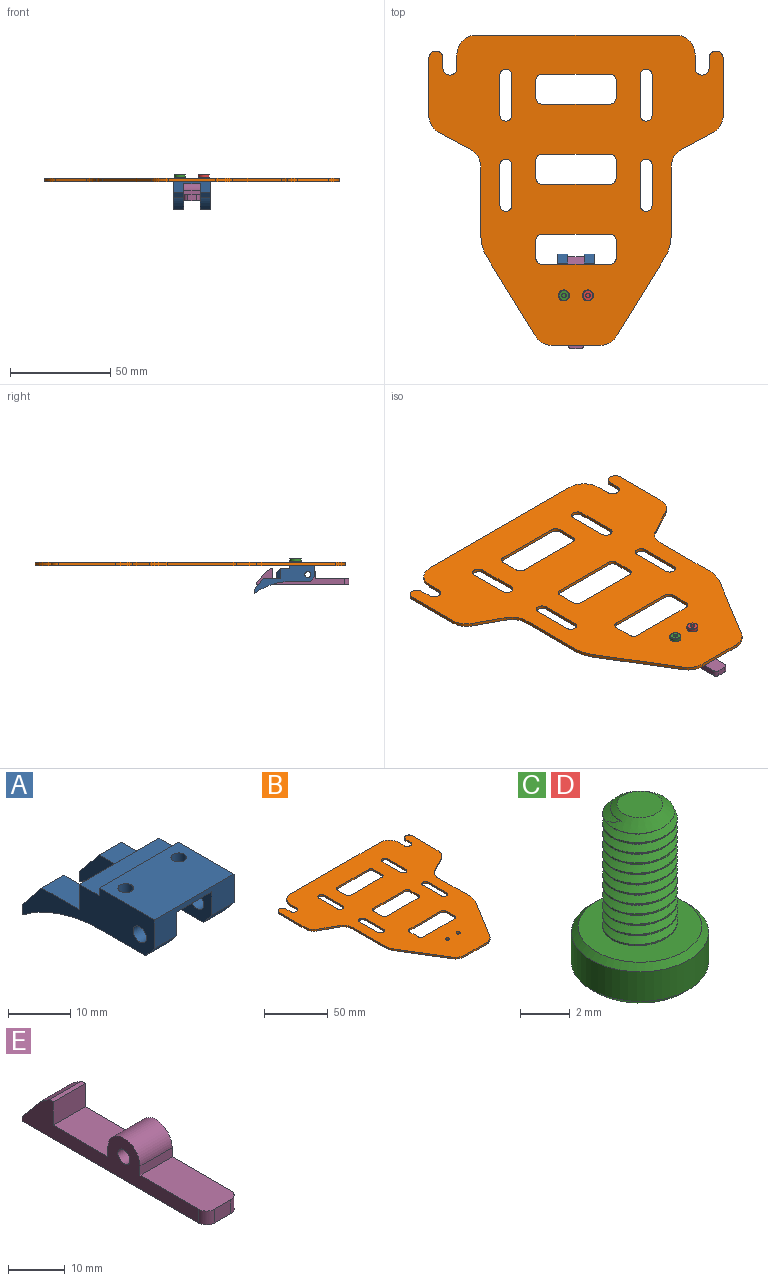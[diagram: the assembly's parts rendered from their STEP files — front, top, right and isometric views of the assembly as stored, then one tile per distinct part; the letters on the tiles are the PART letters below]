
ASSEMBLY  parts=5 mates=3
PART A: 31 faces, bbox 18x30x14 mm
  f0: plane 8.5x5mm, normal (0,0,1), area 34.5mm2, adj f4,f9,f20,f25,f29
  f1: plane 5x2.38mm, normal (0,-0.77,-0.64), area 15.6mm2, adj f2,f6,f20,f25
  f2: plane 10x5mm, normal (0,0,-1), area 45.1mm2, adj f1,f7,f20,f25,f27
  f3: plane 5x2mm, normal (0,1,0), area 10mm2, adj f4,f7,f20,f25
  f4: plane 5.5x5mm, normal (0,0.77,0.63), area 35.5mm2, adj f0,f3,f20,f25
  f5: cylinder r=1.5mm len=5mm, axis (-1,0,0), area 47.1mm2, adj f20,f25
  f6: plane 18x5.62mm, normal (0,-1,0), area 64.2mm2, adj f1,f12,f13,f19,f20,f21,f24,f25
  f7: cylinder r=30mm len=18mm, axis (-1,0,0), area 96.5mm2, adj f2,f3,f20,f25
  f8: plane 8.5x5mm, normal (0,0,1), area 34.5mm2, adj f9,f17,f19,f24,f28
  f9: plane 14x3mm, normal (0,1,0), area 42mm2, adj f0,f8,f22,f28,f29,f30
  f10: plane 18x4.5mm, normal (0,0,1), area 81mm2, adj f11,f19,f20,f30
  f11: plane 18x1.5mm, normal (0,1,0), area 27mm2, adj f10,f12,f19,f20
  f12: plane 18x12.5mm, normal (0,0,1), area 215.2mm2, adj f6,f11,f19,f20,f26,f27
  f13: plane 5x2.38mm, normal (0,-0.77,-0.64), area 15.6mm2, adj f6,f14,f19,f24
  f14: plane 10x5mm, normal (0,0,-1), area 45.1mm2, adj f13,f15,f19,f24,f26
  f15: cylinder r=30mm len=18mm, axis (-1,0,0), area 96.5mm2, adj f14,f16,f19,f24
  f16: plane 5x2mm, normal (0,1,0), area 10mm2, adj f15,f17,f19,f24
  f17: plane 5.5x5mm, normal (0,0.77,0.63), area 35.5mm2, adj f8,f16,f19,f24
  f18: cylinder r=1.5mm len=5mm, axis (-1,0,0), area 47.1mm2, adj f19,f24
  f19: plane 30x14mm, normal (1,0,0), area 161.3mm2, adj f6,f8,f10,f11,f12,f13,f14,f15
  f20: plane 30x14mm, normal (-1,0,0), area 161.3mm2, adj f0,f1,f2,f3,f4,f5,f6,f7
  f21: plane 10x8mm, normal (0,0,-1), area 80mm2, adj f6,f23,f24,f25
  f22: plane 9x8mm, normal (0,0,-1), area 72mm2, adj f9,f23,f24,f25
  f23: plane 8x5.5mm, normal (0,-1,0), area 44mm2, adj f21,f22,f24,f25
  f24: plane 30x13mm, normal (-1,0,0), area 112.6mm2, adj f6,f8,f13,f14,f15,f16,f17,f18
  f25: plane 30x13mm, normal (1,0,0), area 112.6mm2, adj f0,f1,f2,f3,f4,f5,f6,f7
  f26: cylinder r=1.25mm len=8mm, axis (0,0,1), area 62.8mm2, adj f12,f14
  f27: cylinder r=1.25mm len=8mm, axis (0,0,1), area 62.8mm2, adj f2,f12
  f28: plane 5x2mm, normal (0.71,0.71,0), area 11.3mm2, adj f8,f9,f19,f30
  f29: plane 5x2mm, normal (-0.71,0.71,0), area 11.3mm2, adj f0,f9,f20,f30
  f30: plane 18x2mm, normal (0,0.71,0.71), area 45.3mm2, adj f9,f10,f28,f29
PART B: 72 faces, bbox 147x155x1.6 mm
  f0: cylinder r=3mm len=6mm, axis (0,0,-1), area 14.6mm2, adj f1,f67,f68,f69
  f1: plane 20x1.55mm, normal (-1,0,0), area 31mm2, adj f0,f2,f68,f69
  f2: cylinder r=3mm len=6mm, axis (0,0,-1), area 14.6mm2, adj f1,f67,f68,f69
  f3: plane 20x1.55mm, normal (-1,0,0), area 31mm2, adj f4,f60,f68,f69
  f4: cylinder r=3mm len=6mm, axis (0,0,-1), area 14.6mm2, adj f3,f5,f68,f69
  f5: plane 20x1.55mm, normal (1,0,0), area 31mm2, adj f4,f60,f68,f69
  f6: plane 20x1.55mm, normal (-1,0,0), area 31mm2, adj f7,f61,f68,f69
  f7: cylinder r=3mm len=6mm, axis (0,0,-1), area 14.6mm2, adj f6,f8,f68,f69
  f8: plane 20x1.55mm, normal (1,0,0), area 31mm2, adj f7,f61,f68,f69
  f9: cylinder r=10mm len=8.53mm, axis (0,0,-1), area 15.8mm2, adj f10,f62,f68,f69
  f10: plane 39.41x24.13mm, normal (0.85,-0.52,0), area 71.6mm2, adj f9,f11,f68,f69
  f11: cylinder r=20mm len=10.44mm, axis (0,0,-1), area 17mm2, adj f10,f12,f68,f69
  f12: plane 34.39x1.55mm, normal (1,0,0), area 53.3mm2, adj f11,f13,f68,f69
  f13: cylinder r=10mm len=8.8mm, axis (0,0,-1), area 16.7mm2, adj f12,f14,f68,f69
  f14: plane 15.48x8.34mm, normal (0.47,-0.88,0), area 27.3mm2, adj f13,f15,f68,f69
  f15: cylinder r=10mm len=8.8mm, axis (0,0,-1), area 16.7mm2, adj f14,f16,f68,f69
  f16: plane 28.53x1.55mm, normal (1,0,0), area 44.2mm2, adj f15,f17,f68,f69
  f17: cylinder r=3.5mm len=7mm, axis (0,0,-1), area 17mm2, adj f16,f18,f68,f69
  f18: plane 5x1.55mm, normal (-1,0,0), area 7.7mm2, adj f17,f19,f68,f69
  f19: cylinder r=3.5mm len=7mm, axis (0,0,-1), area 17mm2, adj f18,f20,f68,f69
  f20: plane 6.5x1.55mm, normal (1,0,0), area 10.1mm2, adj f19,f21,f68,f69
  f21: cylinder r=10mm len=10mm, axis (0,0,-1), area 24.3mm2, adj f20,f22,f68,f69
  f22: plane 99x1.55mm, normal (0,1,0), area 153.5mm2, adj f21,f23,f68,f69
  f23: cylinder r=10mm len=10mm, axis (0,0,-1), area 24.3mm2, adj f22,f24,f68,f69
  f24: plane 6.5x1.55mm, normal (-1,0,0), area 10.1mm2, adj f23,f25,f68,f69
  f25: cylinder r=3.5mm len=7mm, axis (0,0,-1), area 17mm2, adj f24,f26,f68,f69
  f26: plane 5x1.55mm, normal (1,0,0), area 7.7mm2, adj f25,f27,f68,f69
  f27: cylinder r=3.5mm len=7mm, axis (0,0,-1), area 17mm2, adj f26,f28,f68,f69
  f28: plane 28.53x1.55mm, normal (-1,0,0), area 44.2mm2, adj f27,f29,f68,f69
  f29: cylinder r=10mm len=8.8mm, axis (0,0,-1), area 16.7mm2, adj f28,f30,f68,f69
  f30: plane 15.48x8.34mm, normal (-0.47,-0.88,0), area 27.3mm2, adj f29,f31,f68,f69
  f31: cylinder r=10mm len=8.8mm, axis (0,0,-1), area 16.7mm2, adj f30,f32,f68,f69
  f32: plane 34.39x1.55mm, normal (-1,0,0), area 53.3mm2, adj f31,f33,f68,f69
  f33: cylinder r=20mm len=10.44mm, axis (0,0,-1), area 17mm2, adj f32,f34,f68,f69
  f34: plane 39.41x24.13mm, normal (-0.85,-0.52,0), area 71.6mm2, adj f33,f35,f68,f69
  f35: cylinder r=10mm len=8.53mm, axis (0,0,-1), area 15.8mm2, adj f34,f62,f68,f69
  f36: plane 34x1.55mm, normal (0,1,0), area 52.7mm2, adj f37,f63,f68,f69
  f37: cylinder r=3mm len=3mm, axis (0,0,-1), area 7.3mm2, adj f36,f38,f68,f69
  f38: plane 9x1.55mm, normal (1,0,0), area 14mm2, adj f37,f39,f68,f69
  f39: cylinder r=3mm len=3mm, axis (0,0,-1), area 7.3mm2, adj f38,f40,f68,f69
  f40: plane 34x1.55mm, normal (0,-1,0), area 52.7mm2, adj f39,f41,f68,f69
  f41: cylinder r=3mm len=3mm, axis (0,0,-1), area 7.3mm2, adj f40,f42,f68,f69
  f42: plane 9x1.55mm, normal (-1,0,0), area 14mm2, adj f41,f63,f68,f69
  f43: cylinder r=3mm len=6mm, axis (0,0,-1), area 14.6mm2, adj f44,f64,f68,f69
  f44: plane 20x1.55mm, normal (-1,0,0), area 31mm2, adj f43,f45,f68,f69
  f45: cylinder r=3mm len=6mm, axis (0,0,-1), area 14.6mm2, adj f44,f64,f68,f69
  f46: cylinder r=3mm len=3mm, axis (0,0,-1), area 7.3mm2, adj f47,f65,f68,f69
  f47: plane 9x1.55mm, normal (-1,0,0), area 13.9mm2, adj f46,f48,f68,f69
  f48: cylinder r=3mm len=3mm, axis (0,0,-1), area 7.3mm2, adj f47,f49,f68,f69
  f49: plane 34x1.55mm, normal (0,1,0), area 52.7mm2, adj f48,f50,f68,f69
  f50: cylinder r=3mm len=3mm, axis (0,0,-1), area 7.3mm2, adj f49,f51,f68,f69
  f51: plane 9x1.55mm, normal (1,0,0), area 13.9mm2, adj f50,f52,f68,f69
  f52: cylinder r=3mm len=3mm, axis (0,0,-1), area 7.3mm2, adj f51,f65,f68,f69
  f53: cylinder r=3mm len=3mm, axis (0,0,-1), area 7.3mm2, adj f54,f66,f68,f69
  f54: plane 9x1.55mm, normal (-1,0,0), area 13.9mm2, adj f53,f55,f68,f69
  f55: cylinder r=3mm len=3mm, axis (0,0,-1), area 7.3mm2, adj f54,f56,f68,f69
  f56: plane 34x1.55mm, normal (0,1,0), area 52.7mm2, adj f55,f57,f68,f69
  f57: cylinder r=3mm len=3mm, axis (0,0,-1), area 7.3mm2, adj f56,f58,f68,f69
  f58: plane 9x1.55mm, normal (1,0,0), area 13.9mm2, adj f57,f59,f68,f69
  f59: cylinder r=3mm len=3mm, axis (0,0,-1), area 7.3mm2, adj f58,f66,f68,f69
  f60: cylinder r=3mm len=6mm, axis (0,0,-1), area 14.6mm2, adj f3,f5,f68,f69
  f61: cylinder r=3mm len=6mm, axis (0,0,-1), area 14.6mm2, adj f6,f8,f68,f69
  f62: plane 23.79x1.55mm, normal (0,-1,0), area 36.9mm2, adj f9,f35,f68,f69
  f63: cylinder r=3mm len=3mm, axis (0,0,-1), area 7.3mm2, adj f36,f42,f68,f69
  f64: plane 20x1.55mm, normal (1,0,0), area 31mm2, adj f43,f45,f68,f69
  f65: plane 34x1.55mm, normal (0,-1,0), area 52.7mm2, adj f46,f52,f68,f69
  f66: plane 34x1.55mm, normal (0,-1,0), area 52.7mm2, adj f53,f59,f68,f69
  f67: plane 20x1.55mm, normal (1,0,0), area 31mm2, adj f0,f2,f68,f69
  f68: plane 155x147mm, normal (0,0,1), area 13173.4mm2, adj f0,f1,f2,f3,f4,f5,f6,f7
  f69: plane 155x147mm, normal (0,0,-1), area 13173.4mm2, adj f0,f1,f2,f3,f4,f5,f6,f7
  f70: cylinder r=1.65mm len=3.3mm, axis (0,0,-1), area 16.1mm2, adj f68,f69
  f71: cylinder r=1.65mm len=3.3mm, axis (0,0,-1), area 16.1mm2, adj f68,f69
PART C: 24 faces, bbox 5.9x5.9x8.4 mm
  f0: cone r=2.75mm half-angle=45deg, axis (0,0,-1), area 6.4mm2, adj f3,f11
  f1: cone r=2.48mm half-angle=45deg, axis (0,0,1), area 6.4mm2, adj f3,f10
  f2: cone r=1.15mm half-angle=45deg, axis (0,0,-1), area 0.1mm2, adj f10,f22
  f3: cylinder r=2.75mm len=5.5mm, axis (0,0,1), area 25.1mm2, adj f0,f1
  f4: cone r=0.92mm half-angle=55deg, axis (0,0,-1), area 3.7mm2, adj f5,f6,f7,f8,f9
  f5: cylinder r=1.18mm len=5.82mm, axis (0,0,-1), area 5.4mm2, adj f4,f7,f8,f11
  f6: cylinder r=1.5mm len=5.59mm, axis (0,0,1), area 6.6mm2, adj f4,f7,f8,f11
  f7: bspline ~6.2x3mm, area 36mm2, adj f4,f5,f6,f11
  f8: bspline ~6.01x2.99mm, area 36mm2, adj f4,f5,f6,f11
  f9: plane 1.84x1.84mm, normal (0,0,1), area 2.7mm2, adj f4
  f10: plane 4.95x4.95mm, normal (0,0,-1), area 15.1mm2, adj f1,f2,f12,f13,f14,f15,f16
  f11: plane 5.15x5.15mm, normal (0,0,1), area 13.6mm2, adj f0,f5,f6,f7,f8
  f12: cone r=1.15mm half-angle=45deg, axis (0,0,-1), area 0mm2, adj f10,f18
  f13: cone r=1.15mm half-angle=45deg, axis (0,0,-1), area 0mm2, adj f10,f19
  f14: cone r=1.15mm half-angle=45deg, axis (0,0,-1), area 0mm2, adj f10,f20
  f15: cone r=1.15mm half-angle=45deg, axis (0,0,-1), area 0mm2, adj f10,f21
  f16: cone r=1.15mm half-angle=45deg, axis (0,0,-1), area 0mm2, adj f10,f23
  f17: plane 2.31x2mm, normal (0,0,-1), area 3.5mm2, adj f18,f19,f20,f21,f22,f23
  f18: plane 1.94x1.44mm, normal (-0.5,-0.87,0), area 1.6mm2, adj f12,f17,f19,f23
  f19: plane 1.94x1.59mm, normal (-1,0,0), area 1.6mm2, adj f13,f17,f18,f20
  f20: plane 1.94x1.44mm, normal (-0.5,0.87,0), area 1.6mm2, adj f14,f17,f19,f21
  f21: plane 1.94x1.44mm, normal (0.5,0.87,0), area 1.6mm2, adj f15,f17,f20,f22
  f22: plane 1.61x1.27mm, normal (1,0,0), area 1.6mm2, adj f2,f17,f21,f23
  f23: plane 1.94x1.44mm, normal (0.5,-0.87,0), area 1.6mm2, adj f16,f17,f18,f22
PART D: same geometry as C
PART E: 17 faces, bbox 8x46x9 mm
  f0: cylinder r=4mm len=8mm, axis (-1,0,0), area 100.5mm2, adj f1,f12,f13,f14
  f1: plane 8x2mm, normal (0,-1,0), area 16mm2, adj f0,f2,f13,f14
  f2: plane 16.6x8mm, normal (0,0,1), area 131.1mm2, adj f1,f3,f13,f14,f15,f16
  f3: plane 4x3mm, normal (0,-1,0), area 12mm2, adj f2,f4,f15,f16
  f4: plane 46x8mm, normal (0,0,-1), area 366.3mm2, adj f3,f5,f13,f14,f15,f16
  f5: plane 8x1mm, normal (0,1,0), area 8mm2, adj f4,f6,f13,f14
  f6: plane 8x5.51mm, normal (0,0.77,0.64), area 57.6mm2, adj f5,f7,f13,f14
  f7: plane 8x2.12mm, normal (0,0.57,0.82), area 20.7mm2, adj f6,f8,f13,f14
  f8: plane 8x1mm, normal (0,0,1), area 8mm2, adj f7,f9,f13,f14
  f9: plane 8x5mm, normal (0,-1,0), area 40mm2, adj f8,f10,f13,f14
  f10: plane 13.65x8mm, normal (0,0,1), area 109.2mm2, adj f9,f12,f13,f14
  f11: cylinder r=1.5mm len=8mm, axis (-1,0,0), area 75.4mm2, adj f13,f14
  f12: plane 8x2mm, normal (0,1,0), area 16mm2, adj f0,f10,f13,f14
  f13: plane 44x9mm, normal (1,0,0), area 183.6mm2, adj f0,f1,f2,f4,f5,f6,f7,f8
  f14: plane 44x9mm, normal (-1,0,0), area 183.6mm2, adj f0,f1,f2,f4,f5,f6,f7,f8
  f15: cylinder r=2mm len=3mm, axis (0,0,-1), area 9.4mm2, adj f2,f3,f4,f14
  f16: cylinder r=2mm len=3mm, axis (0,0,1), area 9.4mm2, adj f2,f3,f4,f13
PLACE A at identity
PLACE B at identity fixed
PLACE C rot(axis=(1,0,0),180deg) t=(-6.03,24.94,-4.45)mm
PLACE D rot(axis=(1,0,0),180deg) t=(5.97,24.94,-4.45)mm
PLACE E at identity
MATE fastened B.f70 <-> C.f11  axis (0,0,1) through (-6,25,1.55)mm
MATE revolute E.f0 <-> A.f5  axis (-1,0,0) through (0,18.85,-4.5)mm
MATE fastened B.f71 <-> D.f11  axis (0,0,1) through (6,25,1.55)mm
